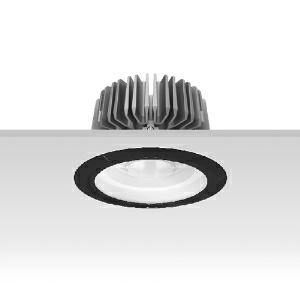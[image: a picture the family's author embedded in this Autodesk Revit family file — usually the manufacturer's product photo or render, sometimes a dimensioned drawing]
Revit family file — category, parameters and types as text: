
# Revit family: 3f_filippi_-_3f_reno_bianco_ampio_3f_filippi_-_30353_a01024_-_3f_reno_150_wh_3000-930_wide___vt_bk_675a
name_source: partatom
category: Lighting Fixtures
units: mm (PartAtom-declared; Revit-internal decimal feet)

## family parameters
Cut with Voids When Loaded = No
Host = Face
Light Source = No
Part Type = Normal
Room Calculation Point = No
Round Connector Dimension = Use Diameter
Shared = No

## types (1)
- 3F Filippi - 3F Reno Bianco Ampio (1 x LED, 2656 lm, 37 W, 3000 K)
    Apparent Load = 37 VA
    Approval mark = CE
    CIE Flux Codes = 74 93 99 100 100
    Color Rendering = 90
    Color Temperature = 3000 K
    Control Gear = Electronic ballast
    Default Elevation = 1800 mm
    Description = ILLUMINOTECHNICAL
Luminous efficiency 100% (DLOR 100%, ULOR 0%).
Initial luminous flux of the luminaire 2656 lm.
Direct symmetric wide distribution.
Installation Interdistance Transv.D = 1.54 x hu - Long.D = 1.54 x hu.
Tabular UGR (CIE 117 - 4H-8H; S=0.25H; 70/50/20): RUG 24.4 - 24.2.
Beam angle: 74° - 73°.
Luminous efficacy 72 lm/W.
Lifetime (L90/B10): 30000 h. (tq+25°C)
Lifetime (L85/B10): 50000 h. (tq+25°C)
Lifetime (L70/B10): 80000 h. (tq+25°C)
Sudden decreased luminous flux after 50000 hours: 0% (C0).
Photobiological safety in compliance with IEC/TR 62778: RG0 risk exempt, (IEC 62471).
In compliance with IEC/EN 62722-2-1 - IEC/EN 62717 standards.

SOURCE
Compact LED module 3000/930.
Energy efficiency class (UE 2019/2020 - UE 2019/2015): E.
CIE 13.3 Colour rendering index: CRI >90 (R9 >50%).
IES TM-30 Fidelity Index: Rf = 92 Rg = 101.
CCT nominal colour temperature 3000 K.
Colour initial tolerance (MacAdam): SDCM 3.
Zhaga Book 3 compliant.

MECHANICAL
Passive heat dissipator in die-casting aluminium, oversized, for optimum thermal management of the LED module.
Parabolic element with graduated/concentric rings in white polycarbonate.
Transparent external lens with glossy and satin differentiated surfaces, with a cooling and anti-insect system in methacrylate (PMMA).
Fastening spring clips in stainless steel.
Dimensions: diameter 176 mm, height 111 mm. Weight 1.455 kg.
IP44 protection degree for exposed part, IP20 for recessed part.
Mechanical strength to impacts IK06 (1 joule).
Glow-wire test resistance 650°C.

ELECTRICAL
Wiring on a separate unit.
Halogen Free electronic wiring 230V-50/60Hz, power factor 0.95, THD <25%, constant output current, SELV, class II, 1 driver.
Power of the luminaire 37 W.
ENEC - CE.
SAFE FLICKER: PstLM=<1 and SVM=<0.4 (IEC TR 61547-1 and IEC TR 63158), to ensure a more comfortable and safe light.
Luminaire compliant with EN 60598-2-22 for power supply from a centralised emergency system CPSS (Central Power Supply System), not incorporated in the luminaire - high risk areas excluded. The default power and flux are 100% in AC and 100% in DC.
Ambient temperature from 0°C to +25°C.
Temperature class T6 max 85°C.
Relative humidity UR: <85%.

INSTALLATION
Pull-up recessed fitting.
False ceiling carving: 150 mm.
All accessories dedicated to this product are available on the Catalog and on our website www.3F-Filippi.com.

ACCESSORIES
A01024 - VT transparent glass, tempered, not flammable, locked and in line with the trim, in black polycarbonate.

APPLICATIONS
Environments: architectural, commercial, exhibition areas, transit areas, corridors, shops, display windows, service areas.
In false ceilings with narrow voids.

WARNING
Luminaire designed for disposal/recycling at end-of-life.
Replaceable (LED only) light source by a professional. Replaceable control gear by a professional.
    Height = 0 mm  [stored 0 ft]
    Lamp = 1 x LED
    Lamp Light Flux = 2656 lm
    Lamp Power = 37 W
    Lamp count = 1
    Length = 176 mm
    Lifetime = 50000 h
    Luminous efficacy = 72 lm/W
    Manufacturer = 3F Filippi
    ModVariant = No
    Model = 3F Filippi - 30353+A01024 - 3F Reno 150 WH 3000-930 WIDE + VT BK
    Mounting Place = Ceiling
    Mounting Type = Recessed
    Number of Poles = 1
    OnlyDefault = Yes
    Power Factor = 1
    Product Name = 3F Filippi - 3F Reno Bianco Ampio
    Product group = recessed luminaire
    ProductGroupID = 4
    Protection Class = Protection class II
    Protection Degree = IP 20
    RLX_Detail_Level = 1
    RLX_Emergency_Light_Flux = 0 lm
    RLX_Emergency_Type = 0
    RLX_Emergency_Type_DB = No
    RlxData = <blob elided: 88757 chars, md5=fafd027b>
    Socket = socket
    Standby Power = 0 W
    System Light Flux = 2656 lm
    System Power = 37 W
    Type Comments = Product without accessories
    Type Image = 3ffilippi_3f_reno_150_wh_d150__a01024.jpg
    URL = http://relux.com
    VarID = ---
    Voltage = 0 V
    Weight = 0.00 kg
    Width = 0 mm  [stored 0 ft]

note: [stored X ft] marks values corroborated as IEEE doubles in the binary element streams (Revit-internal decimal feet)

## geometry (parser evidence)
native form markers: Blend x4, Sweep x11
no freeform markers — native parametric forms only
